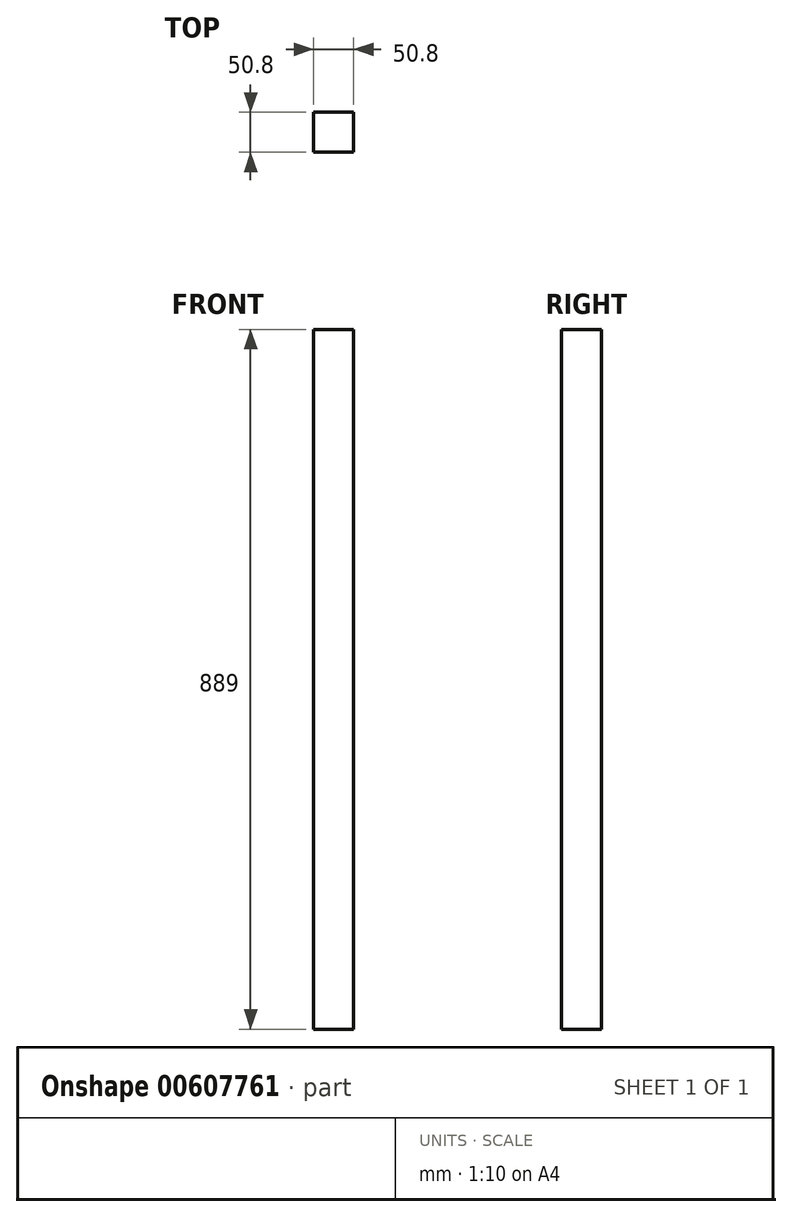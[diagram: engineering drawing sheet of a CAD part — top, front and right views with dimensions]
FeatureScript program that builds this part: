
annotation { "Feature Type Name" : "Feature", "Feature Type Description" : "" }
export const myFeature = defineFeature(function(context is Context, id is Id, definition is map)
    precondition{}
    {
        {
            var Q0;
            Q0=qCreatedBy(makeId("Front.planeOp"),FACE);
            var sketch = newSketch(context, id + "F0", { "sketchPlane" : qUnion([Q0])});
            skLineSegment(sketch, "E0", {"start": v(0, 0) * mm, "end": v(0, -889) * mm});
            skLineSegment(sketch, "E1", {"start": v(0, -889) * mm, "end": v(-50.8, -889) * mm});
            skLineSegment(sketch, "E2", {"start": v(-50.8, -889) * mm, "end": v(-50.8, 0) * mm});
            skLineSegment(sketch, "E3", {"start": v(-50.8, 0) * mm, "end": v(0, 0) * mm});
            skSolve(sketch);
        }
        {
            var Q0;
            Q0 = qSketchRegion(id + "F0", true);
            extrude(context, id + "F1", {"entities" : qUnion([Q0]), "depth" : 50.8 * mm, "offsetDistance" : 25.4 * mm});
        }
    });
